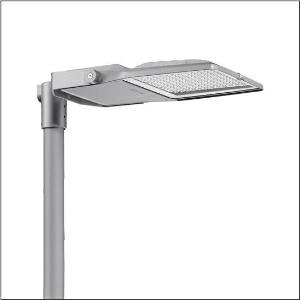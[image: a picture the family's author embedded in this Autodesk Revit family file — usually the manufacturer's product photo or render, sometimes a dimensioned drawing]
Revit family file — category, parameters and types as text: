
# Revit family: floodlight_fl_21_iq_midi___pl52_5xa7781e4d3a_f0c1
name_source: partatom
category: Lighting Fixtures
units: mm (PartAtom-declared; Revit-internal decimal feet)

## family parameters
Cut with Voids When Loaded = No
Host = Face
Light Source = No
Part Type = Normal
Room Calculation Point = No
Round Connector Dimension = Use Diameter
Shared = No

## types (1)
- --- (1 x LED, 28010 lm, 208.1 W, 4000K)
    Apparent Load = 208 VA
    CIE Flux Codes = 26 60 98 100 100
    Color Rendering = 70
    Color Temperature = 4000K
    Default Elevation = 1800 mm
    Description = Floodlight FL 21 iQ midi, floodlight, primary light control with lens, of PMMA, primary optical cover: protective disc, of toughened safety glass, transparent, light distribution: PL52, light emission: direct distribution, installation type: surface-mounted, LED, High Power LED, rated luminous flux: 28.010lm, luminous efficacy: 135lm/W, light colour: 740, colour temperature: 4000K, control gear: ECG iQ, control: optimised constant luminous flux control (CLO 2.0), Desk-Remote (wireless, voltage-free reading and setting of iQ features in the workshop via application-optimized NFC function/RFID function), Light-Fading, Smart-Wire, Night-Set, Lumen-Switch, Temp-Guard, Auto-Match, with terminal, 6-pole, mains connection: 220..240V, AC, 50/60Hz, start of lifetime: 208W, end of service life: 227W, reduction: 90W, luminaire housing, of diecast aluminium, powder-coated, Siteco® metallic grey (DB 702S), corrosivity category C5 mid according to DIN EN ISO 12944, sealing non-destructively replaceable, please order mast flange separately, mast bracket, of steel, galvanised, powder-coated, Siteco® metallic grey (DB 702S), protection rating (complete): IP66, insulation class (complete): insulation class II (safety insulation), certification: CE, protection symbol: D, impact resistance: IK08, permissible operating ambient temperature: -40..+40°C, permissible operating ambient temperature for outdoor applications: -40..+50°C, standard: DIN EN 12944, LABS conformity tested according to VDMA 24364:2018-05, packaging unit: 1 piece

Light Distribution: PL52
    Height = 76 mm
    Lamp = 1 x LED
    Lamp Light Flux = 28010 lm
    Lamp Power = 208.1 W
    Lamp count = 1
    Length = 657 mm
    Luminous efficacy = 135 lm/W
    Manufacturer = Siteco
    ModVariant = No
    Model = 5XA7781E4D3A
    Number of Poles = 1
    OnlyDefault = Yes
    Power Factor = 1
    Product Name = Floodlight FL 21 iQ midi | PL52
    Product group = floodlight | pylon annexe
    ProductGroupID = 6200
    Protection Class = Protection class II
    Protection Degree = IP 66
    RLX_Detail_Level = 1
    RLX_Emergency_Light_Flux = 0 lm
    RLX_Emergency_Type = 0
    RLX_Emergency_Type_DB = No
    RlxData = <blob elided: 153769 chars, md5=afe0bce1>
    Socket = socket
    Standby Power = 0 W
    System Light Flux = 28010 lm
    System Power = 208 W
    Type Comments = factory setting: luminous flux: 100 % | dim-lin: 254 | 710 mA
    Type Image = l_1007123.jpg
    URL = http://relux.com
    VarID = @adj_054485
    Voltage = 0 V
    Weight = 0.00 kg
    Width = 442 mm

## geometry (parser evidence)
native form markers: Blend x4, Sweep x15
no freeform markers — native parametric forms only
